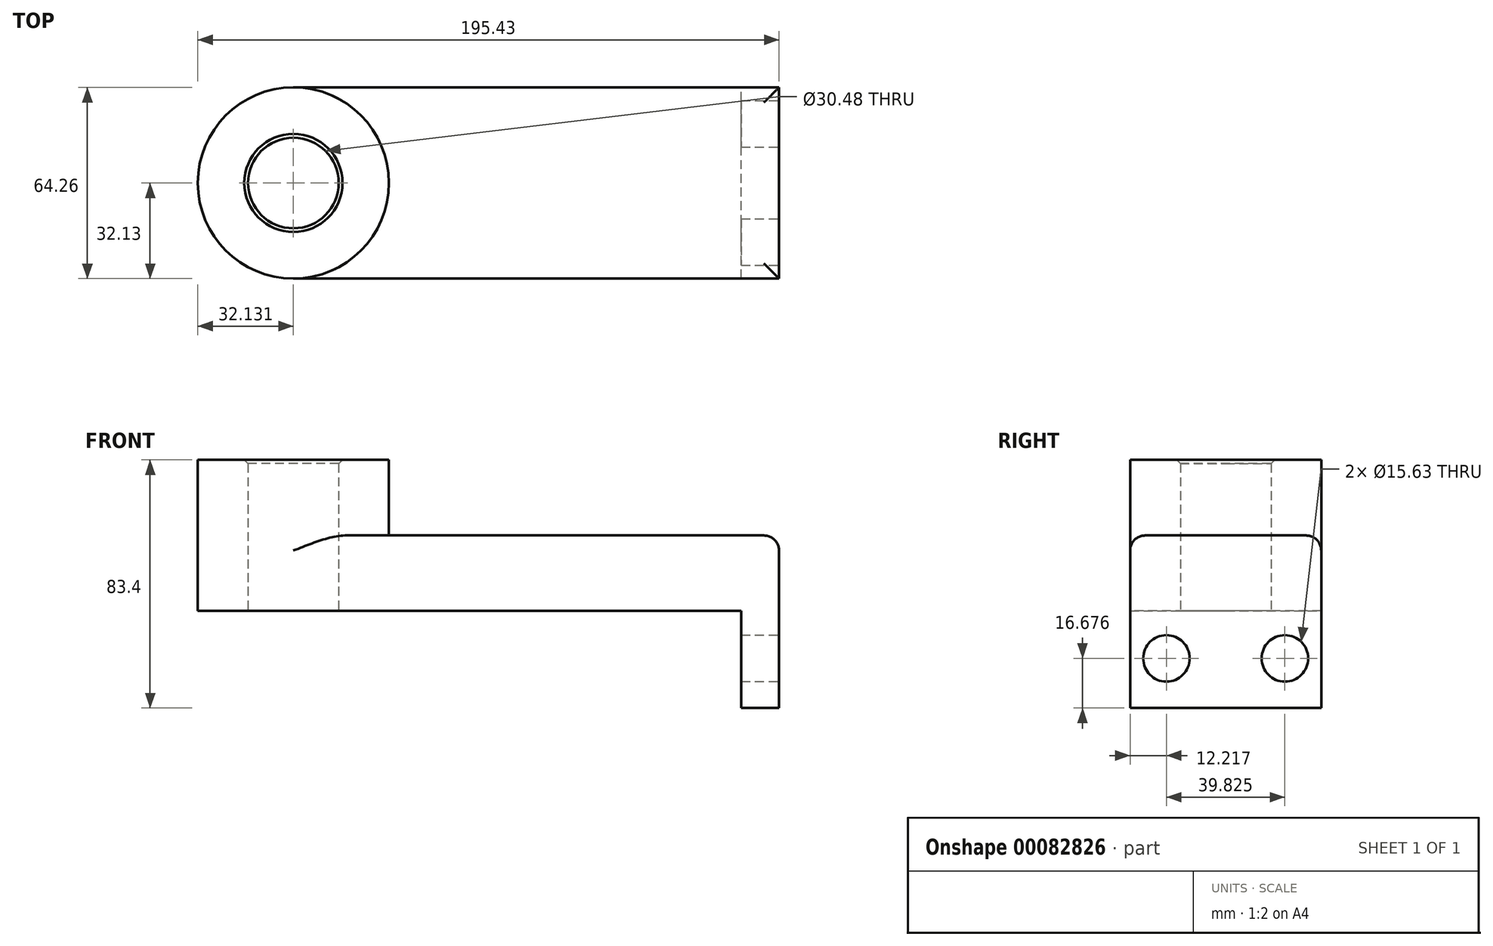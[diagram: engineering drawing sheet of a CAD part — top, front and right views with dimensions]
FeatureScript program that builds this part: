
annotation { "Feature Type Name" : "Feature", "Feature Type Description" : "" }
export const myFeature = defineFeature(function(context is Context, id is Id, definition is map)
    precondition{}
    {
        {
            var Q0;
            Q0=qCreatedBy(makeId("Top.planeOp"),FACE);
            var sketch = newSketch(context, id + "F0", { "sketchPlane" : qUnion([Q0])});
            skLineSegment(sketch, "E0.bottom", {"start": v(81.65, 32.13) * mm, "end": v(-81.65, 32.13) * mm});
            skLineSegment(sketch, "E0.top", {"start": v(81.65, -32.13) * mm, "end": v(-81.65, -32.13) * mm});
            skLineSegment(sketch, "E0.left", {"start": v(81.65, 32.13) * mm, "end": v(81.65, -32.13) * mm});
            skLineSegment(sketch, "E0.right", {"start": v(-81.65, 32.13) * mm, "end": v(-81.65, -32.13) * mm});
            skPoint(sketch, "E0.middle", {"position": v(0, 0) * mm});
            skCircle(sketch, "E1", {"center": v(-81.65, 0) * mm, "radius": 32.13 * mm});
            skCircle(sketch, "E2", {"center": v(-81.65, 0) * mm, "radius": 15.24 * mm});
            skSolve(sketch);
        }
        {
            var Q0;
            {var subQ0=sQuery(id+"F0.wireOp",EDGE,"E0.bottom");Q0=makeQuery(id+"F0.imprint","IMPRINT",FACE,{"disambiguationData":[TD([[makeQuery(id+"F0.imprint","IMPRINT",EDGE,{"derivedFrom":subQ0}),1.0]])]});}
            var Q1;
            {var subQ1=sQuery(id+"F0.wireOp",EDGE,"E0.right");var subQ3=sQuery(id+"F0.wireOp",EDGE,"E2");var subQ4=makeQuery(id+"F0.imprint","INTERSECT",VERTEX,{"disambiguationData":[OD(0.0)],"derivedFrom":[subQ1,subQ3]});Q1=makeQuery(id+"F0.imprint","IMPRINT",FACE,{"disambiguationData":[TD([[makeQuery(id+"F0.imprint","IMPRINT",EDGE,{"disambiguationData":[TD([[subQ4,-1.0]])],"derivedFrom":subQ3}),-1.0]])]});}
            var Q2;
            {var subQ1=sQuery(id+"F0.wireOp",EDGE,"E0.right");var subQ3=sQuery(id+"F0.wireOp",EDGE,"E2");var subQ4=makeQuery(id+"F0.imprint","INTERSECT",VERTEX,{"disambiguationData":[OD(0.0)],"derivedFrom":[subQ1,subQ3]});Q2=makeQuery(id+"F0.imprint","IMPRINT",FACE,{"disambiguationData":[TD([[makeQuery(id+"F0.imprint","IMPRINT",EDGE,{"disambiguationData":[TD([[subQ4,1.0]])],"derivedFrom":subQ3}),-1.0]])]});}
            extrude(context, id + "F1", {"entities" : qUnion([Q0, Q1, Q2]), "depth" : 25.4 * mm});
        }
        {
            var Q0;
            {var subQ1=sQuery(id+"F0.wireOp",EDGE,"E0.right");var subQ3=sQuery(id+"F0.wireOp",EDGE,"E2");var subQ4=makeQuery(id+"F0.imprint","INTERSECT",VERTEX,{"disambiguationData":[OD(0.0)],"derivedFrom":[subQ1,subQ3]});Q0=makeQuery(id+"F0.imprint","IMPRINT",FACE,{"disambiguationData":[TD([[makeQuery(id+"F0.imprint","IMPRINT",EDGE,{"disambiguationData":[TD([[subQ4,-1.0]])],"derivedFrom":subQ3}),-1.0]])]});}
            var Q1;
            {var subQ1=sQuery(id+"F0.wireOp",EDGE,"E0.right");var subQ3=sQuery(id+"F0.wireOp",EDGE,"E2");var subQ4=makeQuery(id+"F0.imprint","INTERSECT",VERTEX,{"disambiguationData":[OD(0.0)],"derivedFrom":[subQ1,subQ3]});Q1=makeQuery(id+"F0.imprint","IMPRINT",FACE,{"disambiguationData":[TD([[makeQuery(id+"F0.imprint","IMPRINT",EDGE,{"disambiguationData":[TD([[subQ4,1.0]])],"derivedFrom":subQ3}),-1.0]])]});}
            extrude(context, id + "F2", {"entities" : qUnion([Q0, Q1]), "operationType" : NewBodyOperationType.ADD, "depth" : 50.8 * mm});
        }
        {
            var Q0;
            Q0=makeQuery(id+"F1.opExtrude","SWEPT_FACE",FACE,{"disambiguationData":[OSD([sQuery(id+"F0.wireOp",EDGE,"E0.left")])]});
            var sketch = newSketch(context, id + "F3", { "sketchPlane" : qUnion([Q0])});
            skLineSegment(sketch, "E3.bottom", {"start": v(32.13, 25.4) * mm, "end": v(-32.13, 25.4) * mm});
            skLineSegment(sketch, "E3.top", {"start": v(32.13, -32.6) * mm, "end": v(-32.13, -32.6) * mm});
            skLineSegment(sketch, "E3.left", {"start": v(32.13, 25.4) * mm, "end": v(32.13, -32.6) * mm});
            skLineSegment(sketch, "E3.right", {"start": v(-32.13, 25.4) * mm, "end": v(-32.13, -32.6) * mm});
            skCircle(sketch, "E4", {"center": v(-19.91, -15.92) * mm, "radius": 7.82 * mm});
            skLineSegment(sketch, "E5", {"start": v(0, 0) * mm, "end": v(0, -32.6) * mm, "construction": true});
            skCircle(sketch, "E6.MirrorC", {"center": v(19.91, -15.92) * mm, "radius": 7.82 * mm});
            skSolve(sketch);
        }
        {
            var Q0;
            Q0 = qSketchRegion(id + "F3", true);
            extrude(context, id + "F4", {"entities" : qUnion([Q0]), "operationType" : NewBodyOperationType.ADD, "oppositeDirection" : true, "depth" : 12.7 * mm});
        }
        {
            var Q0;
            Q0=makeQuery(id+"F1.opExtrude","CAP_EDGE",EDGE,{"disambiguationData":[OSD([sQuery(id+"F0.wireOp",EDGE,"E0.top")])],"isStart":false});
            var Q1;
            Q1=makeQuery(id+"F1.opExtrude","CAP_EDGE",EDGE,{"disambiguationData":[OSD([sQuery(id+"F0.wireOp",EDGE,"E0.bottom")])],"isStart":false});
            var Q2;
            Q2=makeQuery(id+"F1.opExtrude","CAP_EDGE",EDGE,{"disambiguationData":[OSD([sQuery(id+"F0.wireOp",EDGE,"E0.left")])],"isStart":false});
            fillet(context, id + "F5", {"entities" : qUnion([Q0, Q1, Q2]), "radius" : 5.08 * mm, "tangentPropagation" : true, "allowEdgeOverflow" : false});
        }
        {
            var Q0;
            Q0=makeQuery(id+"F2.opExtrude","CAP_EDGE",EDGE,{"disambiguationData":[OSD([sQuery(id+"F0.wireOp",EDGE,"E2")])],"isStart":false});
            chamfer(context, id + "F6", {"entities" : qUnion([Q0]), "width" : 1.27 * mm, "tangentPropagation" : true});
        }
    });
